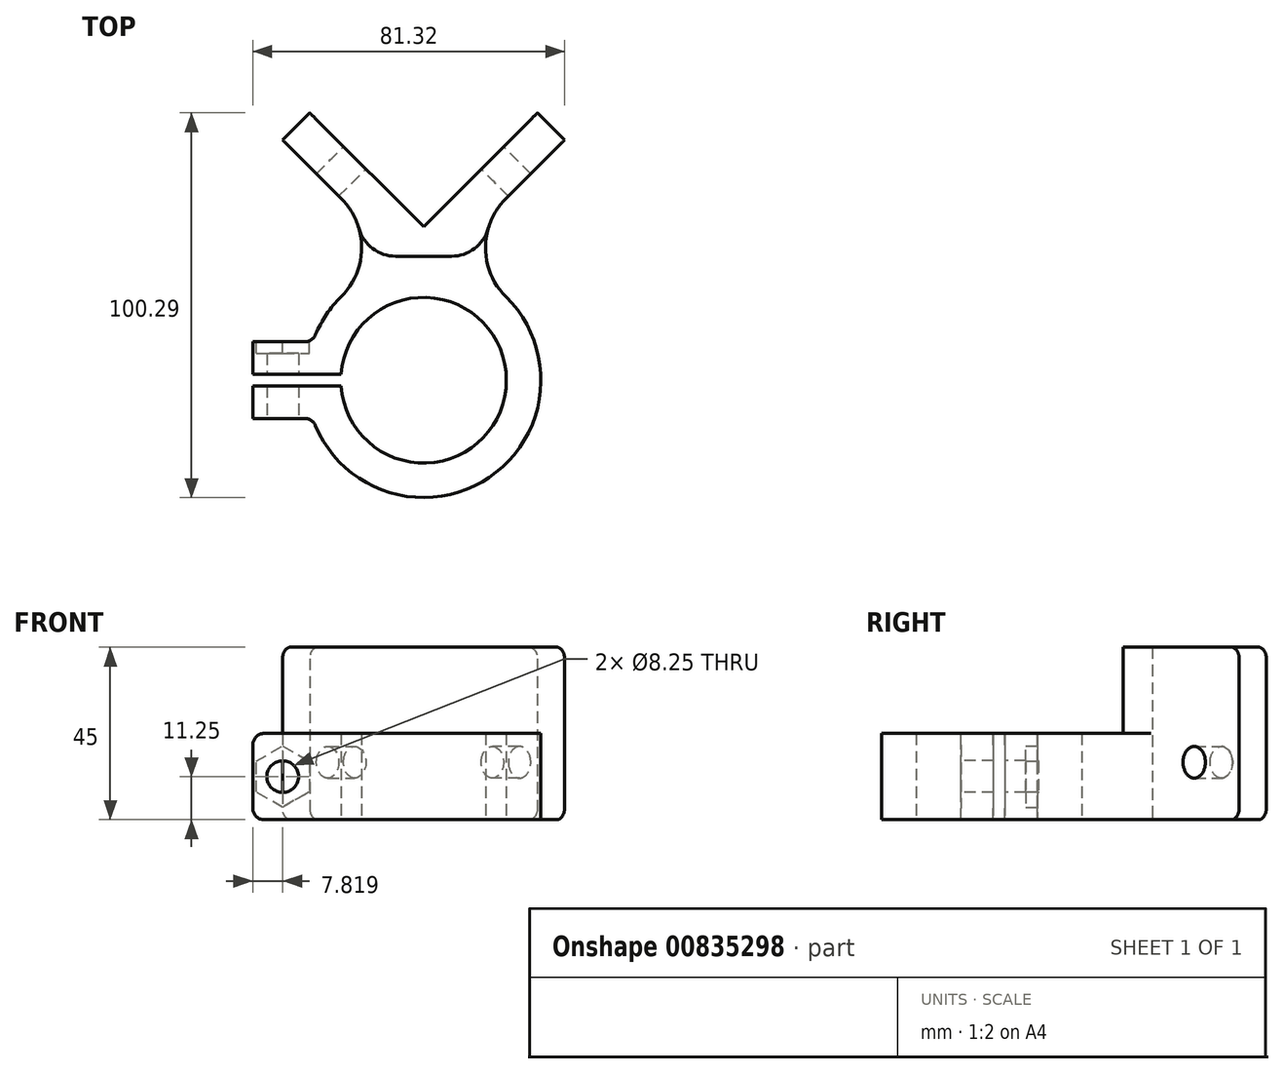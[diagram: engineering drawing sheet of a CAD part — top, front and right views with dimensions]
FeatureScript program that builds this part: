
annotation { "Feature Type Name" : "Feature", "Feature Type Description" : "" }
export const myFeature = defineFeature(function(context is Context, id is Id, definition is map)
    precondition{}
    {
        {
            var Q0;
            Q0=qCreatedBy(makeId("Top.planeOp"),FACE);
            var sketch = newSketch(context, id + "F0", { "sketchPlane" : qUnion([Q0])});
            skLineSegment(sketch, "E0", {"start": v(0, 0) * mm, "end": v(-29.7, 29.7) * mm});
            skLineSegment(sketch, "E1", {"start": v(0, 38.94) * mm, "end": v(0, 0) * mm, "construction": true});
            skLineSegment(sketch, "E2", {"start": v(-29.7, 29.7) * mm, "end": v(-36.77, 22.63) * mm});
            skLineSegment(sketch, "E3", {"start": v(-36.77, 22.63) * mm, "end": v(-4.41, -9.73) * mm});
            skLineSegment(sketch, "E4", {"start": v(0, 0) * mm, "end": v(0, -40) * mm, "construction": true});
            skArc(sketch, "E5", {"start": v(-21.54, -41.5) * mm, "mid": v(21.6, -40) * mm, "end": v(-21.54, -38.5) * mm});
            skArc(sketch, "E6", {"start": v(-30.55, -41.5) * mm, "mid": v(20.57, -62.64) * mm, "end": v(4.41, -9.73) * mm});
            skLineSegment(sketch, "E7", {"start": v(0, -40) * mm, "end": v(-30.59, -40) * mm, "construction": true});
            skLineSegment(sketch, "E8", {"start": v(-30.55, -38.5) * mm, "end": v(-44.55, -38.5) * mm});
            skLineSegment(sketch, "E9", {"start": v(-44.55, -38.5) * mm, "end": v(-44.55, -30) * mm});
            skLineSegment(sketch, "E10", {"start": v(-44.55, -30) * mm, "end": v(-28.9, -30) * mm});
            skLineSegment(sketch, "E11.MirrorCS", {"start": v(-44.55, -41.5) * mm, "end": v(-44.55, -50) * mm});
            skLineSegment(sketch, "E12.MirrorCS", {"start": v(-44.55, -50) * mm, "end": v(-28.9, -50) * mm});
            skLineSegment(sketch, "E13.MirrorCS", {"start": v(-30.55, -41.5) * mm, "end": v(-44.55, -41.5) * mm});
            skLineSegment(sketch, "E14", {"start": v(-30.55, -38.5) * mm, "end": v(-21.54, -38.5) * mm});
            skLineSegment(sketch, "E15.MirrorCS", {"start": v(-30.55, -41.5) * mm, "end": v(-21.54, -41.5) * mm});
            skLineSegment(sketch, "E16.MirrorCS", {"start": v(29.7, 29.7) * mm, "end": v(36.77, 22.63) * mm});
            skLineSegment(sketch, "E17.MirrorCS", {"start": v(0, 0) * mm, "end": v(29.7, 29.7) * mm});
            skLineSegment(sketch, "E18.MirrorCS", {"start": v(36.77, 22.63) * mm, "end": v(4.41, -9.73) * mm});
            skPoint(sketch, "E19.orphan", {"position": v(0, -14.14) * mm});
            skArc(sketch, "E20.trimOffspring", {"start": v(-4.41, -9.73) * mm, "mid": v(-22.64, -19.43) * mm, "end": v(-30.55, -38.5) * mm});
            skSolve(sketch);
        }
        {
            var Q0;
            Q0=makeQuery(id+"F0.imprint","IMPRINT",FACE,{"disambiguationData":[TD([[makeQuery(id+"F0.imprint","IMPRINT",EDGE,{"derivedFrom":sQuery(id+"F0.wireOp",EDGE,"E0")}),1.0]])]});
            var Q1;
            {var subQ4=sQuery(id+"F0.wireOp",EDGE,"E9");Q1=makeQuery(id+"F0.imprint","IMPRINT",FACE,{"disambiguationData":[TD([[makeQuery(id+"F0.imprint","IMPRINT",EDGE,{"derivedFrom":subQ4}),-1.0]])]});}
            var Q2;
            {var subQ1=sQuery(id+"F0.wireOp",EDGE,"E11.MirrorCS");Q2=makeQuery(id+"F0.imprint","IMPRINT",FACE,{"disambiguationData":[TD([[makeQuery(id+"F0.imprint","IMPRINT",EDGE,{"derivedFrom":subQ1}),1.0]])]});}
            extrude(context, id + "F1", {"entities" : qUnion([Q0, Q1, Q2]), "depth" : 45 * mm, "offsetDistance" : 25 * mm});
        }
        {
            var Q0;
            Q0=makeQuery(id+"F1.opExtrude","SWEPT_FACE",FACE,{"disambiguationData":[OSD([sQuery(id+"F0.wireOp",EDGE,"E17.MirrorCS")])]});
            var sketch = newSketch(context, id + "F2", { "sketchPlane" : qUnion([Q0])});
            skLineSegment(sketch, "E21", {"start": v(0, 15) * mm, "end": v(-50.8, 15) * mm, "construction": true});
            skCircle(sketch, "E22", {"center": v(-25.4, 15) * mm, "radius": 4.12 * mm});
            skSolve(sketch);
        }
        {
            var Q0;
            Q0=qSketchRegion(id+"F2",true);
            extrude(context, id + "F3", {"entities" : qUnion([Q0]), "operationType" : NewBodyOperationType.REMOVE, "endBound" : BoundingType.UP_TO_NEXT, "oppositeDirection" : true, "depth" : 25 * mm, "offsetDistance" : 25 * mm});
        }
        {
            var Q0;
            Q0=makeQuery(id+"F1.opExtrude","SWEPT_FACE",FACE,{"disambiguationData":[OSD([sQuery(id+"F0.wireOp",EDGE,"E0")])]});
            var sketch = newSketch(context, id + "F4", { "sketchPlane" : qUnion([Q0])});
            skLineSegment(sketch, "E23", {"start": v(0, 15) * mm, "end": v(50.8, 15) * mm, "construction": true});
            skCircle(sketch, "E24", {"center": v(25.4, 15) * mm, "radius": 4.12 * mm});
            skSolve(sketch);
        }
        {
            var Q0;
            Q0=qSketchRegion(id+"F4",true);
            extrude(context, id + "F5", {"entities" : qUnion([Q0]), "operationType" : NewBodyOperationType.REMOVE, "endBound" : BoundingType.UP_TO_NEXT, "oppositeDirection" : true, "depth" : 25 * mm, "offsetDistance" : 25 * mm});
        }
        {
            var Q0;
            Q0=makeQuery(id+"F1.opExtrude","SWEPT_FACE",FACE,{"disambiguationData":[OSD([sQuery(id+"F0.wireOp",EDGE,"E12.MirrorCS")])]});
            var sketch = newSketch(context, id + "F6", { "sketchPlane" : qUnion([Q0])});
            skLineSegment(sketch, "E25", {"start": v(-36.73, 45) * mm, "end": v(-36.73, 0) * mm, "construction": true});
            skLineSegment(sketch, "E26", {"start": v(-44.55, 22.5) * mm, "end": v(-28.9, 22.5) * mm, "construction": true});
            skLineSegment(sketch, "E27", {"start": v(-44.55, 22.5) * mm, "end": v(-28.9, 45) * mm, "construction": true});
            skCircle(sketch, "E28", {"center": v(-36.73, 33.75) * mm, "radius": 4.12 * mm});
            skCircle(sketch, "E29.MirrorC", {"center": v(-36.73, 11.25) * mm, "radius": 4.12 * mm});
            skLineSegment(sketch, "E30.MirrorCS", {"start": v(-44.55, 22.5) * mm, "end": v(-28.9, 0) * mm, "construction": true});
            skSolve(sketch);
        }
        {
            var Q0;
            Q0=qSketchRegion(id+"F6",true);
            var Q1;
            Q1=makeQuery(id+"F1.opExtrude","SWEPT_FACE",FACE,{"disambiguationData":[OSD([sQuery(id+"F0.wireOp",EDGE,"E10")])]});
            extrude(context, id + "F7", {"entities" : qUnion([Q0]), "operationType" : NewBodyOperationType.REMOVE, "endBound" : BoundingType.UP_TO_SURFACE, "oppositeDirection" : true, "depth" : 25 * mm, "endBoundEntityFace" : qUnion([Q1]), "offsetDistance" : 25 * mm});
        }
        {
            var Q0;
            Q0=makeQuery(id+"F1.opExtrude","SWEPT_FACE",FACE,{"disambiguationData":[OSD([sQuery(id+"F0.wireOp",EDGE,"E10")])]});
            var sketch = newSketch(context, id + "F8", { "sketchPlane" : qUnion([Q0])});
            skCircle(sketch, "E31.cCircle", {"center": v(36.73, 33.75) * mm, "radius": 6.92 * mm, "construction": true});
            skLineSegment(sketch, "E31.0", {"start": v(36.73, 41.75) * mm, "end": v(43.66, 37.75) * mm});
            skLineSegment(sketch, "E31.1", {"start": v(43.66, 37.75) * mm, "end": v(43.66, 29.75) * mm});
            skLineSegment(sketch, "E31.2", {"start": v(43.66, 29.75) * mm, "end": v(36.73, 25.75) * mm});
            skLineSegment(sketch, "E31.3", {"start": v(36.73, 25.75) * mm, "end": v(29.8, 29.75) * mm});
            skLineSegment(sketch, "E31.4", {"start": v(29.8, 29.75) * mm, "end": v(29.8, 37.75) * mm});
            skLineSegment(sketch, "E31.5", {"start": v(29.8, 37.75) * mm, "end": v(36.73, 41.75) * mm});
            skPoint(sketch, "E31.0.midPoint", {"position": v(40.2, 39.75) * mm});
            skLineSegment(sketch, "E32", {"start": v(74.38, 22.5) * mm, "end": v(44.55, 22.5) * mm, "construction": true});
            skLineSegment(sketch, "E33.MirrorCS", {"start": v(43.66, 15.25) * mm, "end": v(36.73, 19.25) * mm});
            skLineSegment(sketch, "E34.MirrorCS", {"start": v(29.8, 15.25) * mm, "end": v(29.8, 7.25) * mm});
            skLineSegment(sketch, "E35.MirrorCS", {"start": v(36.73, 3.25) * mm, "end": v(43.66, 7.25) * mm});
            skLineSegment(sketch, "E36.MirrorCS", {"start": v(36.73, 19.25) * mm, "end": v(29.8, 15.25) * mm});
            skCircle(sketch, "E37.MirrorC", {"center": v(36.73, 11.25) * mm, "radius": 6.92 * mm, "construction": true});
            skLineSegment(sketch, "E38.MirrorCS", {"start": v(43.66, 7.25) * mm, "end": v(43.66, 15.25) * mm});
            skLineSegment(sketch, "E39.MirrorCS", {"start": v(29.8, 7.25) * mm, "end": v(36.73, 3.25) * mm});
            skPoint(sketch, "E40.MirrorP", {"position": v(40.2, 5.25) * mm});
            skSolve(sketch);
        }
        {
            var Q0;
            Q0=qSketchRegion(id+"F8",true);
            extrude(context, id + "F9", {"entities" : qUnion([Q0]), "operationType" : NewBodyOperationType.REMOVE, "oppositeDirection" : true, "depth" : 3 * mm, "offsetDistance" : 25 * mm});
        }
        {
            var Q0;
            Q0=makeQuery(id+"F1.opExtrude","SWEPT_EDGE",EDGE,{"disambiguationData":[OSD([sQuery(id+"F0.wireOp",EDGE,"E3"),sQuery(id+"F0.wireOp",EDGE,"E20.trimOffspring")])]});
            var Q1;
            Q1=makeQuery(id+"F1.opExtrude","SWEPT_EDGE",EDGE,{"disambiguationData":[OSD([sQuery(id+"F0.wireOp",EDGE,"E6"),sQuery(id+"F0.wireOp",EDGE,"E18.MirrorCS")])]});
            fillet(context, id + "F10", {"entities" : qUnion([Q0, Q1]), "radius" : 18 * mm, "tangentPropagation" : true, "allowEdgeOverflow" : false});
        }
        {
            var Q0;
            Q0=qCreatedBy(makeId("Right.planeOp"),FACE);
            var sketch = newSketch(context, id + "F11", { "sketchPlane" : qUnion([Q0])});
            skLineSegment(sketch, "E41", {"start": v(-80.12, 22.5) * mm, "end": v(-7.68, 22.5) * mm});
            skLineSegment(sketch, "E42", {"start": v(-7.68, 22.5) * mm, "end": v(-7.68, 58.55) * mm});
            skLineSegment(sketch, "E43", {"start": v(-7.68, 58.55) * mm, "end": v(-80.12, 58.55) * mm});
            skLineSegment(sketch, "E44", {"start": v(-80.12, 58.55) * mm, "end": v(-80.12, 22.5) * mm});
            skSolve(sketch);
        }
        {
            var Q0;
            Q0=qSketchRegion(id+"F11",true);
            extrude(context, id + "F12", {"entities" : qUnion([Q0]), "operationType" : NewBodyOperationType.REMOVE, "endBound" : BoundingType.SYMMETRIC, "oppositeDirection" : true, "depth" : 200 * mm, "offsetDistance" : 25 * mm});
        }
        {
            var Q0;
            Q0=makeQuery(id+"F1.opExtrude","CAP_EDGE",EDGE,{"disambiguationData":[OSD([sQuery(id+"F0.wireOp",EDGE,"E9")])],"isStart":false});
            var Q1;
            Q1=makeQuery(id+"F1.opExtrude","CAP_EDGE",EDGE,{"disambiguationData":[OSD([sQuery(id+"F0.wireOp",EDGE,"E11.MirrorCS")])],"isStart":false});
            var Q2;
            Q2=makeQuery(id+"F1.opExtrude","CAP_EDGE",EDGE,{"disambiguationData":[OSD([sQuery(id+"F0.wireOp",EDGE,"E11.MirrorCS")])],"isStart":true});
            var Q3;
            Q3=makeQuery(id+"F1.opExtrude","CAP_EDGE",EDGE,{"disambiguationData":[OSD([sQuery(id+"F0.wireOp",EDGE,"E9")])],"isStart":true});
            var Q4;
            Q4=makeQuery(id+"F1.opExtrude","CAP_EDGE",EDGE,{"disambiguationData":[OSD([sQuery(id+"F0.wireOp",EDGE,"E2")])],"isStart":false});
            var Q5;
            Q5=makeQuery(id+"F1.opExtrude","CAP_EDGE",EDGE,{"disambiguationData":[OSD([sQuery(id+"F0.wireOp",EDGE,"E16.MirrorCS")])],"isStart":false});
            var Q6;
            Q6=makeQuery(id+"F1.opExtrude","CAP_EDGE",EDGE,{"disambiguationData":[OSD([sQuery(id+"F0.wireOp",EDGE,"E16.MirrorCS")])],"isStart":true});
            var Q7;
            Q7=makeQuery(id+"F1.opExtrude","CAP_EDGE",EDGE,{"disambiguationData":[OSD([sQuery(id+"F0.wireOp",EDGE,"E2")])],"isStart":true});
            var Q8;
            Q8=makeQuery(id+"F1.opExtrude","SWEPT_EDGE",EDGE,{"disambiguationData":[OSD([sQuery(id+"F0.wireOp",EDGE,"E10"),sQuery(id+"F0.wireOp",EDGE,"E20.trimOffspring")])]});
            var Q9;
            Q9=makeQuery(id+"F1.opExtrude","SWEPT_EDGE",EDGE,{"disambiguationData":[OSD([sQuery(id+"F0.wireOp",EDGE,"E6"),sQuery(id+"F0.wireOp",EDGE,"E12.MirrorCS")])]});
            var Q10;
            Q10=makeQuery(id+"F12.boolean.opBoolean","INTERSECT",EDGE,{"derivedFrom":[makeQuery(id+"F1.opExtrude","SWEPT_FACE",FACE,{"disambiguationData":[OSD([sQuery(id+"F0.wireOp",EDGE,"E9")])]}),makeQuery(id+"F12.opExtrude","SWEPT_FACE",FACE,{"disambiguationData":[OSD([sQuery(id+"F11.wireOp",EDGE,"E41")])]})]});
            var Q11;
            Q11=makeQuery(id+"F12.boolean.opBoolean","INTERSECT",EDGE,{"derivedFrom":[makeQuery(id+"F1.opExtrude","SWEPT_FACE",FACE,{"disambiguationData":[OSD([sQuery(id+"F0.wireOp",EDGE,"E11.MirrorCS")])]}),makeQuery(id+"F12.opExtrude","SWEPT_FACE",FACE,{"disambiguationData":[OSD([sQuery(id+"F11.wireOp",EDGE,"E41")])]})]});
            fillet(context, id + "F13", {"entities" : qUnion([Q0, Q1, Q2, Q3, Q4, Q5, Q6, Q7, Q8, Q9, Q10, Q11]), "radius" : 3 * mm, "tangentPropagation" : true, "allowEdgeOverflow" : false});
        }
        {
            var Q0;
            Q0=makeQuery(id+"F12.boolean.opBoolean","INTERSECT",EDGE,{"derivedFrom":[makeQuery(id+"F10.opFillet","BLEND_FACE",FACE,{"disambiguationData":[OSD([sQuery(id+"F0.wireOp",EDGE,"E3"),sQuery(id+"F0.wireOp",EDGE,"E20.trimOffspring")])]}),makeQuery(id+"F12.opExtrude","SWEPT_FACE",FACE,{"disambiguationData":[OSD([sQuery(id+"F11.wireOp",EDGE,"E42")])]})]});
            var Q1;
            Q1=makeQuery(id+"F12.boolean.opBoolean","INTERSECT",EDGE,{"derivedFrom":[makeQuery(id+"F10.opFillet","BLEND_FACE",FACE,{"disambiguationData":[OSD([sQuery(id+"F0.wireOp",EDGE,"E6"),sQuery(id+"F0.wireOp",EDGE,"E18.MirrorCS")])]}),makeQuery(id+"F12.opExtrude","SWEPT_FACE",FACE,{"disambiguationData":[OSD([sQuery(id+"F11.wireOp",EDGE,"E42")])]})]});
            fillet(context, id + "F14", {"entities" : qUnion([Q0, Q1]), "radius" : 10 * mm, "tangentPropagation" : true, "allowEdgeOverflow" : false});
        }
    });
